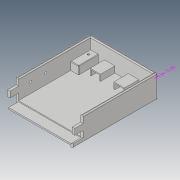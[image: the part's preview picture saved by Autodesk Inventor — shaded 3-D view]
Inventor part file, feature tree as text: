
AUTODESK INVENTOR PART (.ipt)
format: ipt  version: 2019 (Build 230136000, 136)  size: 402,432 bytes
history: native  units: mm
features: extrude x10, sketch x10, other x6, projected_geometry x5, fillet x2, plane x2, surface_op x1
ambient origin geometry x8: Origin, YZ Plane, XZ Plane, XY Plane, X Axis, Y Axis, Z Axis, Center Point
bodies: Solid1 (feature_tree)
feature tree (36):
  other  "Annotations"
  extrude  "Extrusion1"  Depth=170.0mm
  extrude  "Extrusion2"  Depth=5.0mm
  extrude  "Extrusion3"  Depth=25.0mm TaperAngle=0.0deg
  fillet  "Fillet1"  Radius=2.0mm
  extrude  "Extrusion4"  TaperAngle=0.0deg  [1 undecoded]
  extrude  "Extrusion5"  Depth=40.0mm
  fillet  "Fillet2"  [1 undecoded]
  plane  "Work Plane2"
  extrude  "Extrusion7"  Depth=35.0mm
  plane  "Work Plane1"
  extrude  "Extrusion8"  Depth=16.0mm TaperAngle=0.0deg
  surface_op  "Sculpt3"
  extrude  "Extrusion9"  Depth=6.0mm
  extrude  "Extrusion10"  Depth=7.0mm
  extrude  "Extrusion11"  Depth=1.0mm
  sketch  "Sketch1"  dims[d0=135.0mm d1=170.0mm]
  sketch  "Sketch2"  dims[d2=46.7mm d3=0.0mm d4=5.0mm]
  projected_geometry  "Projected Loop1"
  sketch  "Sketch3"  dims[d5=38.7mm d6=0.0mm d7=25.0mm d8=0.0mm d9=2.0mm]
  projected_geometry  "Projected Loop2"
  sketch  "Sketch4"  dims[d10=0.0mm d11=0.0mm]
  sketch  "Sketch5"  dims[d12=16.0mm d13=40.0mm d14=0.0mm]
  sketch  "Sketch6"  dims[d15=0.0mm d16=35.0mm]
  sketch  "Sketch7"  dims[d17=16.0mm d18=16.0mm d19=0.0mm]
  sketch  "Sketch8"  dims[d20=4.5mm d22=6.0mm]
  sketch  "Sketch9"  dims[d23=4.5mm d24=7.0mm]
  projected_geometry  "Projected Loop3"
  sketch  "Sketch10"  dims[d26=12.0mm d27=0.0mm d28=1.0mm d29=4.5mm d30=4.5mm d31=30.8mm d34=90.0mm d37=0.0mm d38=0.0mm d39=-1.5mm d40=7.5mm d41=7.5mm d42=3.15mm d43=0.0mm d44=10.0mm d45=12.5mm d46=18.0mm d50=30.0mm d51=17.0mm d52=10.5mm d54=10.5mm d55=17.0mm d56=10.5mm d57=29.0mm d58=0.0mm d61=1.1mm d62=1.1mm d63=2.2mm d64=2.2mm d65=9.4mm d66=0.0mm d67=9.4mm d68=0.0mm d47=3.35283mm d48=6.847037mm d49=5.0mm]
  projected_geometry  "Projected Loop4"
  projected_geometry  "Projected Loop5"
  other  "Composite3"
  other  "Srf3"
  other  "Linear Dimension 1"
  other  "Assembly1"
  other  "Case_B1:1"
note: 2 required parameter values undecoded (feature->parameter linkage not recoverable at this tier; creation-order binding heuristic only, values carry confidence <= 0.55)
